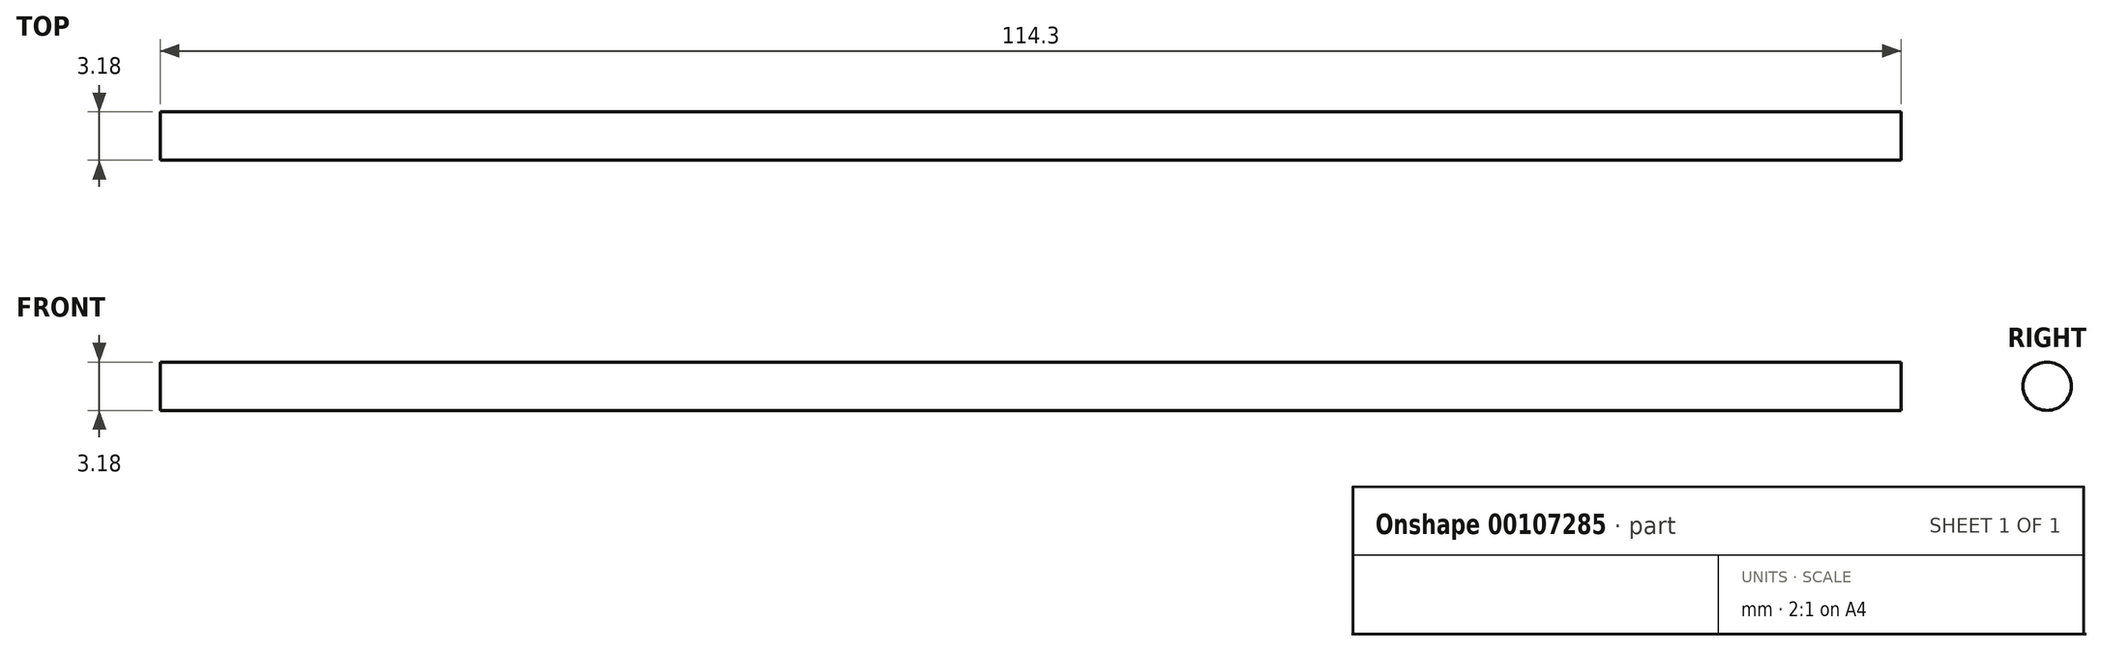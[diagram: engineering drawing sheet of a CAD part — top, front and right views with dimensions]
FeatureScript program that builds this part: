
annotation { "Feature Type Name" : "Feature", "Feature Type Description" : "" }
export const myFeature = defineFeature(function(context is Context, id is Id, definition is map)
    precondition{}
    {
        {
            var Q0;
            Q0=qCreatedBy(makeId("Right.planeOp"),FACE);
            var sketch = newSketch(context, id + "F0", { "sketchPlane" : qUnion([Q0])});
            skCircle(sketch, "E0", {"center": v(0, 0) * mm, "radius": 1.59 * mm});
            skSolve(sketch);
        }
        {
            var Q0;
            Q0=makeQuery(id+"F0.imprint","IMPRINT",FACE,{"disambiguationData":[TD([[makeQuery(id+"F0.imprint","IMPRINT",EDGE,{"derivedFrom":sQuery(id+"F0.wireOp",EDGE,"E0")}),1.0]])]});
            extrude(context, id + "F1", {"entities" : qUnion([Q0]), "depth" : 114.3 * mm});
        }
    });
